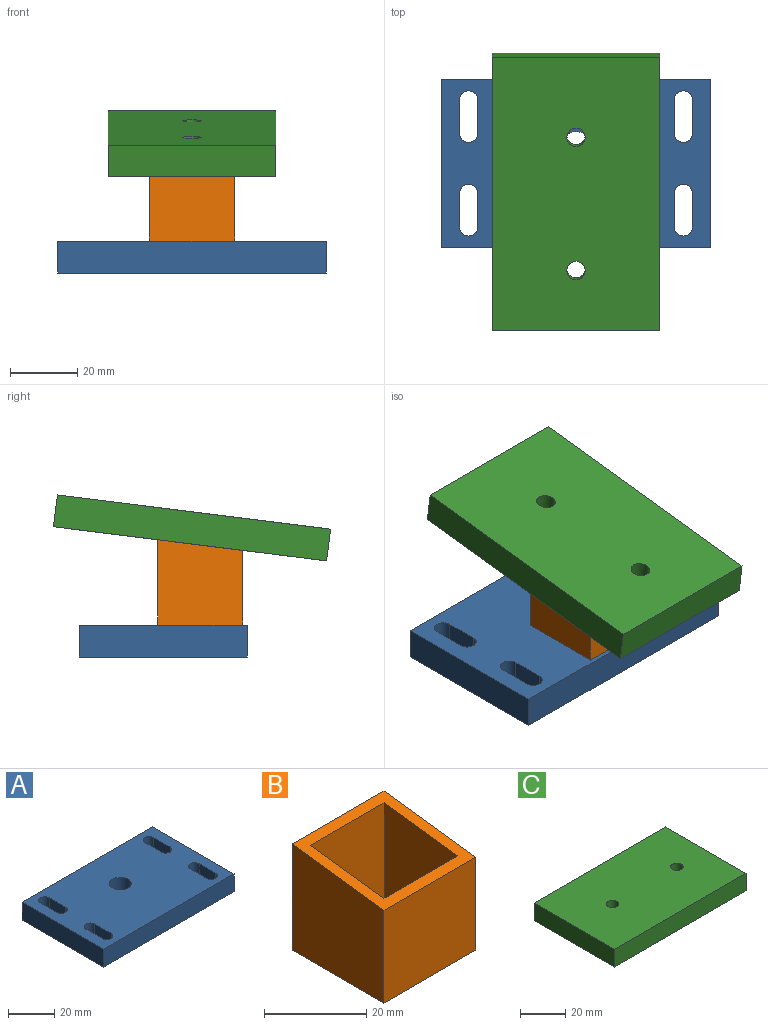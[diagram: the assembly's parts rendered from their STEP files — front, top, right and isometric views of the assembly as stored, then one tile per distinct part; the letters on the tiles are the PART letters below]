
ASSEMBLY  parts=3 mates=2
PART A: 23 faces, bbox 80x50x9.5 mm
  f0: plane 80x9.53mm, normal (0,-1,0), area 762mm2, adj f1,f3,f4,f5
  f1: plane 50x9.53mm, normal (1,0,0), area 476.2mm2, adj f0,f2,f4,f5
  f2: plane 80x9.53mm, normal (0,1,0), area 762mm2, adj f1,f3,f4,f5
  f3: plane 50x9.53mm, normal (-1,0,0), area 476.2mm2, adj f0,f2,f4,f5
  f4: plane 80x50mm, normal (0,0,1), area 3621.1mm2, adj f0,f1,f2,f3,f6,f7,f8,f9
  f5: plane 80x50mm, normal (0,0,-1), area 3621.1mm2, adj f0,f1,f2,f3,f6,f7,f8,f9
  f6: plane 10x9.53mm, normal (-1,0,0), area 95.3mm2, adj f4,f5,f7,f9
  f7: cylinder r=2.7mm len=9.53mm, axis (0,0,1), area 80.8mm2, adj f4,f5,f6,f8
  f8: plane 10x9.53mm, normal (1,0,0), area 95.3mm2, adj f4,f5,f7,f9
  f9: cylinder r=2.7mm len=9.53mm, axis (0,0,1), area 80.8mm2, adj f4,f5,f6,f8
  f10: plane 10x9.53mm, normal (1,0,0), area 95.3mm2, adj f4,f5,f11,f13
  f11: cylinder r=2.7mm len=9.53mm, axis (0,0,1), area 80.8mm2, adj f4,f5,f10,f12
  f12: plane 10x9.53mm, normal (-1,0,0), area 95.3mm2, adj f4,f5,f11,f13
  f13: cylinder r=2.7mm len=9.53mm, axis (0,0,1), area 80.8mm2, adj f4,f5,f10,f12
  f14: plane 10x9.53mm, normal (1,0,0), area 95.3mm2, adj f4,f5,f15,f17
  f15: cylinder r=2.7mm len=9.53mm, axis (0,0,1), area 80.8mm2, adj f4,f5,f14,f16
  f16: plane 10x9.53mm, normal (-1,0,0), area 95.3mm2, adj f4,f5,f15,f17
  f17: cylinder r=2.7mm len=9.53mm, axis (0,0,1), area 80.8mm2, adj f4,f5,f14,f16
  f18: plane 10x9.53mm, normal (-1,0,0), area 95.3mm2, adj f4,f5,f19,f21
  f19: cylinder r=2.7mm len=9.53mm, axis (0,0,1), area 80.8mm2, adj f4,f5,f18,f20
  f20: plane 10x9.53mm, normal (1,0,0), area 95.3mm2, adj f4,f5,f19,f21
  f21: cylinder r=2.7mm len=9.53mm, axis (0,0,1), area 80.8mm2, adj f4,f5,f18,f20
  f22: cylinder r=4.76mm len=9.53mm, axis (0,0,1), area 285mm2, adj f4,f5
PART B: 10 faces, bbox 25.4x25.4x25.4 mm
  f0: plane 25.4x25.4mm, normal (1,0,0), area 604.8mm2, adj f1,f3,f4,f9
  f1: plane 25.4x25.4mm, normal (0,0,-1), area 232.3mm2, adj f0,f2,f3,f4,f5,f6,f7,f8
  f2: plane 25.4x25.4mm, normal (-1,0,0), area 604.8mm2, adj f1,f3,f4,f9
  f3: plane 25.4x22.23mm, normal (0,-1,0), area 564.5mm2, adj f0,f1,f2,f9
  f4: plane 25.4x25.4mm, normal (0,1,0), area 645.2mm2, adj f0,f1,f2,f9
  f5: plane 25.08x20.32mm, normal (-1,0,0), area 483.9mm2, adj f1,f7,f8,f9
  f6: plane 25.08x20.32mm, normal (1,0,0), area 483.9mm2, adj f1,f7,f8,f9
  f7: plane 22.54x20.32mm, normal (0,1,0), area 458.1mm2, adj f1,f5,f6,f9
  f8: plane 25.08x20.32mm, normal (0,-1,0), area 509.7mm2, adj f1,f5,f6,f9
  f9: plane 25.4x25.4mm, normal (0,-0.12,0.99), area 234.1mm2, adj f0,f2,f3,f4,f5,f6,f7,f8
PART C: 12 faces, bbox 82x50x9.5 mm
  f0: plane 82x9.53mm, normal (0,-1,0), area 781.1mm2, adj f1,f3,f4,f5
  f1: plane 50x9.53mm, normal (1,0,0), area 476.3mm2, adj f0,f2,f4,f5
  f2: plane 82x9.53mm, normal (0,1,0), area 781.1mm2, adj f1,f3,f4,f5
  f3: plane 50x9.53mm, normal (-1,0,0), area 476.3mm2, adj f0,f2,f4,f5
  f4: plane 82x50mm, normal (0,0,1), area 4052.5mm2, adj f0,f1,f2,f3,f6,f9
  f5: plane 82x50mm, normal (0,0,-1), area 3950.7mm2, adj f0,f1,f2,f3,f8,f11
  f6: cylinder r=2.75mm len=5.5mm, axis (0,0,-1), area 78.2mm2, adj f4,f7
  f7: plane 9.75x9.75mm, normal (0,0,-1), area 50.9mm2, adj f6,f8
  f8: cylinder r=4.88mm len=9.75mm, axis (0,0,-1), area 153.2mm2, adj f5,f7
  f9: cylinder r=2.75mm len=5.5mm, axis (0,0,-1), area 78.2mm2, adj f4,f10
  f10: plane 9.75x9.75mm, normal (0,0,-1), area 50.9mm2, adj f9,f11
  f11: cylinder r=4.88mm len=9.75mm, axis (0,0,-1), area 153.2mm2, adj f5,f10
PLACE A t=(0.65,55.77,9.05)mm
PLACE B t=(0.65,44.75,31.28)mm
PLACE C rot(axis=(0.06,0.06,-1),90.2deg) t=(0.65,47.79,42.77)mm
MATE fastened B.f1 <-> A.f4  axis (0,0,-1) through (0.65,44.75,18.58)mm
MATE fastened C.f5 <-> B.f9  axis (0,0.12,-0.99) through (0.65,47.91,42.78)mm
